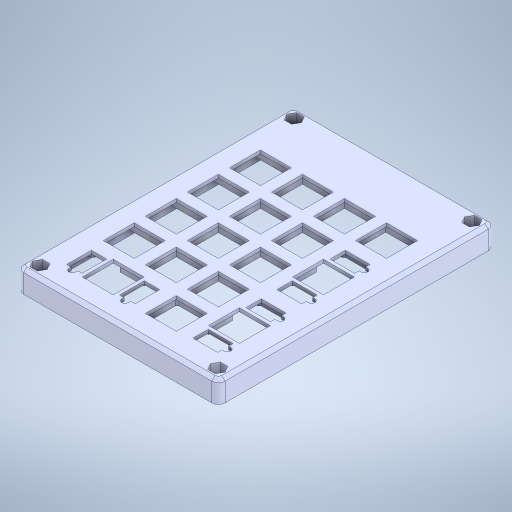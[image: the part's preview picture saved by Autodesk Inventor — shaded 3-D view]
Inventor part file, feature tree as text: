
AUTODESK INVENTOR PART (.ipt)
format: ipt  version: 2024 (Build 280153020, 153B)  size: 851,968 bytes
history: native  units: in
note: dims shown in document units (in); Inventor stores cm internally (conversion verified against a paired STEP export)
features: sketch x5, extrude x3, direct_edit x2, move_body x2, other x1
ambient origin geometry x8: Origin, YZ Plane, XZ Plane, XY Plane, X Axis, Y Axis, Z Axis, Center Point
bodies: Solid1 (feature_tree)
feature tree (13):
  extrude  "Extrusion1"  Depth=0.1378in TaperAngle=0.0deg
  direct_edit  "Direct Edit1"
  direct_edit  "Direct Edit2"
  sketch  "Sketch2"  dims[d8=0.015in d9=0.0in d10=0.0in d12=0.0591in]
  sketch  "Sketch3"  dims[d13=0.0591in d14=0.0591in]
  extrude  "Extrusion2"  Depth=0.0591in
  extrude  "Extrusion3"  Depth=0.0591in
  sketch  "Sketch1"  dims[d3=0.1378in d4=0.0in d5=0.015in d6=0.0in d7=0.0in]
  sketch  "Sketch4"  dims[d15=0.0591in]
  sketch  "Sketch5"  dims[d16=0.0591in d17=0.0591in d18=0.1378in d19=0.0in d32=0.1378in d33=0.0in d27=0.0197in d28=1.9685in d29=0.0197in d30=1.9685in]
  other  "Raccordo2"
  move_body  "Move1"
  move_body  "Move2"
